# Revit family: PRD_AR_MxrTps_ThermostaticSingle-leverPillarMixer_F5LT1010_F5LT1011
name_source: partatom
category: Plumbing Fixtures
units: mm (PartAtom-declared; Revit-internal decimal feet)

## family parameters
Always vertical = Yes
Cut with Voids When Loaded = No
OmniClass Number = 23.45.55.17
OmniClass Title = Mixing Faucets
Part Type = Normal
Room Calculation Point = No
Round Connector Dimension = Use Diameter
Shared = No
Work Plane-Based = No

## types (2) — shared parameters
AccentColour = none
AssetType = Fixed
BasicColour = chrome-look (glossy)
BodyMaterial = PRD_AR_ChromatedBrass_HighPolished
CalculationFlowRateColdWater = 0.07 l/s
CalculationFlowRateHotWater = 0.07 l/s
Category = Pr_40_20_87_55, Mixer taps
CloseOffRating = 0.0 Pa
Color = chrome-look (glossy)
Depressurised = no
DiameterNominal = 15 mm
DurationUnit = year
FaucetFunction = Mixed
FaucetOperation = LeverHandle
FaucetType = Pillar
Finish = polished chrome-plated
FlowColdWater = 0.1 L/s
FlowHotWater = 0.1 L/s
FunctionalPrinciple = manual
HygieneFlushing = prepared
IfcExportAs = IfcValveType
IfcExportType = FAUCET
LockingMechanism = Top section, ceramic
Manufacturer = KWC Group AG
ManufacturerName = KWC Group AG
ManufacturerURL = www.kwc.com
Material = Brass
MaterialFitting = brass-look
MinimumFlowPressure = 1 bar
NBSDescription = Taps and water supply fittings for sinks
NBSReference = 45-35-70/345
NominalHeight = 173 mm  [stored 0.567585 ft]
NominalWidth = 50 mm  [stored 0.164042 ft]
Pop-upWasteSet = no
ProductInformation = http://pim.kwc.com
ProtectiveShutdown = no
Shape = Pillar tap
Size = 15
SoundInsulation = no
Spout = fixed
SpoutProjection = 125 mm
Status = New
SurfaceFinishFitting = chromed
SurfaceTreatmentFitting = polished
TailorMade = no
TemperatureLimit = yes
TestPressure = 0.0 Pa
ThermalDisinfection = yes
TypeOfMixing = with thermostat
TypeOfMounting = tap hole
TypeOfOperation = manual operation
TypeOfTap = pillar tap
URL = www.kwc.com
Uniclass2015Code = Pr_40_20_87_55
Uniclass2015Title = Mixer taps
Uniclass2015Version = Products v1.32
ValveMechanism = OTHER
ValveOperation = LEVER
ValvePattern = STRAIGHT_3_PORT
Version = 1
VolumeFlowRate = 0.1 l/s at 3 bar
WarrantyDurationUnit = year
WithBackflowPreventer = no
WithFilter = yes
WithRosettesOrCoverPlate = no
WorkingPressure = 0.0 Pa
zero-valued in all types: Default Elevation, FlowCoefficient, NominalDepth

## per-type parameters (varying)
| type | BIMObjectName | Description | Features | InletSize | ModelNumber | Name | WaterConnection |
| F5LT1010 | PRD_AR_MixerTaps_ThermostaticSingle-leverPillarMixer_F5LT1010 | F5L-Therm thermostatic single-lever mixer as DN 15 pillar mixer for accessible sanitary facilities, lever length 150 mm. Thermostatically-controlled mixer cartridge with expansion element and active scald protection as well as adjustable and turn-proof temperature stop, and ceramic disc technology. With mechanism for optional hygiene unit for automatic hygiene flushing and program-controlled thermal disinfection and storage of statistical data. Lever cap in ergonomic bracket design, with slight curvature in the front and basalt-grey coating, in line with two-senses principle (tactile and visual). For connection to hot water and cold water via hoses, includes strainers. All-metal construction, high-polished chrome-plated brass. Laminar jet regulator with integrated flow rate. | For connection to hot water and cold water via hoses, includes strainers. Lever length 150 mm. | G 3/8 | 2030066301 | F5L-Therm thermostatic single-lever pillar mixer, barrier-free F5LT1010 | hose (gland nut) |
| F5LT1011 | PRD_AR_MixerTaps_ThermostaticSingle-leverPillarMixer_F5LT1011 | F5L-Therm thermostatic single-lever mixer as DN 15 pillar mixer for accessible sanitary facilities, lever length 150 mm. Thermostatically-controlled mixer cartridge with expansion element and active scald protection as well as adjustable and turn-proof temperature stop, and ceramic disc technology. With mechanism for optional hygiene unit for automatic hygiene flushing and program-controlled thermal disinfection and storage of statistical data. Lever cap in ergonomic bracket design, with slight curvature in the front and basalt-grey coating, in line with two-senses principle (tactile and visual). For connection to hot water and cold water via pipes, includes strainers. All-metal construction, high-polished chrome-plated brass. Laminar jet regulator with integrated flow rate. | For connection to hot water and cold water via pipes, includes strainers. Lever length 150 mm. | DN 10 | 2030066489 | F5L-Therm thermostatic single-lever pillar mixer, barrier-free F5LT1011 | pipe |

note: column(s) folded — value = type name in every type: Model, ModelReference

note: [stored X ft] marks values corroborated as IEEE doubles in the binary element streams (Revit-internal decimal feet)

## geometry (parser evidence)
native form markers: Sweep x6
no freeform markers — native parametric forms only
